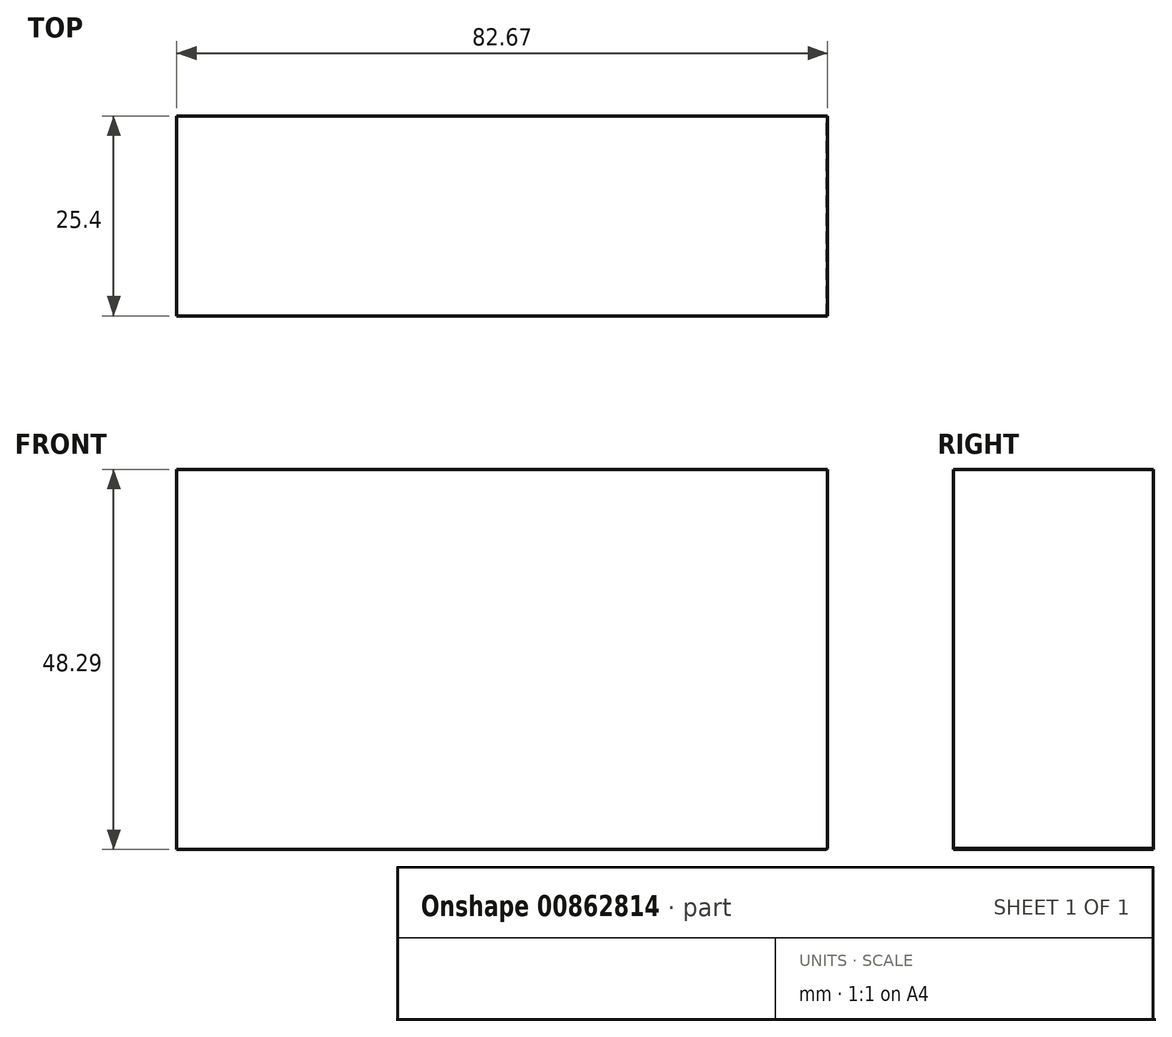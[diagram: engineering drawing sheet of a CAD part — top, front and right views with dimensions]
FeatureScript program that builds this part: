
annotation { "Feature Type Name" : "Feature", "Feature Type Description" : "" }
export const myFeature = defineFeature(function(context is Context, id is Id, definition is map)
    precondition{}
    {
        {
            assignVariable(context, id + "F0", {"name" : "s", "anyValue" : 2});
        }
        {
            var Q0;
            Q0=qCreatedBy(makeId("Front.planeOp"),FACE);
            var sketch = newSketch(context, id + "F1", { "sketchPlane" : qUnion([Q0])});
            skLineSegment(sketch, "E0.bottom", {"start": v(-82.67, 32.22) * mm, "end": v(0, 32.22) * mm});
            skLineSegment(sketch, "E0.top", {"start": v(-82.67, -16.07) * mm, "end": v(0, -16.07) * mm});
            skLineSegment(sketch, "E0.left", {"start": v(-82.67, 32.22) * mm, "end": v(-82.67, -16.07) * mm});
            skLineSegment(sketch, "E0.right", {"start": v(0, 32.22) * mm, "end": v(0, -16.07) * mm});
            skSolve(sketch);
        }
        {
            var Q0;
            Q0 = qSketchRegion(id + "F1", true);
            extrude(context, id + "F2", {"entities" : qUnion([Q0]), "depth" : 25.4 * mm, "offsetDistance" : 25.4 * mm});
        }
        {
            var Q0;
            Q0=sQuery(id+"F1.wireOp",VERTEX,"E0.top.end");
            var Q1;
            Q1=makeQuery(id+"F2.opExtrude","SWEPT_BODY",BODY,{"disambiguationData":[OSD([sQuery(id+"F1.wireOp",EDGE,"E0.bottom"),sQuery(id+"F1.wireOp",EDGE,"E0.top"),sQuery(id+"F1.wireOp",EDGE,"E0.left"),sQuery(id+"F1.wireOp",EDGE,"E0.right")])]});
            hole(context, id + "F3", {"style" : HoleStyle.C_SINK, "endStyle" : HoleEndStyle.THROUGH, "oppositeDirection" : true, "holeDiameter" : (getVariable(context, 's') * 0.12) * mm, "cSinkDiameter" : (getVariable(context, 's') * 0.2) * mm, "cSinkAngle" : 1.57 * radian, "majorDiameter" : 6.35 * mm, "isTappedThrough" : true, "tappedDepth" : 12.7 * mm, "tapClearance" : 3, "locations" : qUnion([Q0]), "scope" : qUnion([Q1])});
        }
    });
